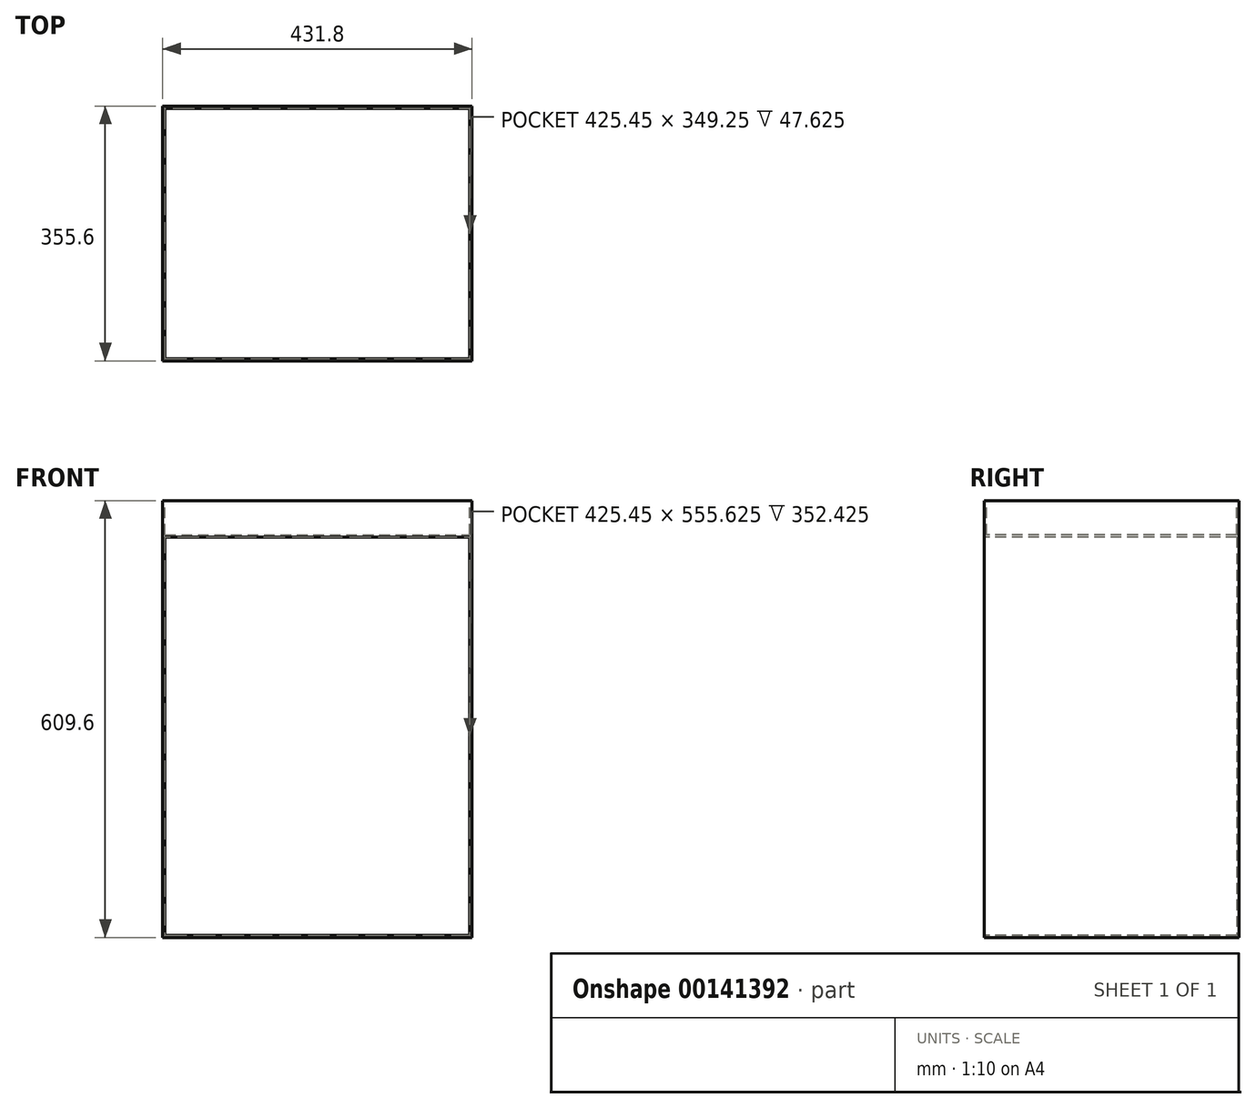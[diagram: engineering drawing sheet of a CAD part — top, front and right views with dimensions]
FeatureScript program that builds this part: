
annotation { "Feature Type Name" : "Feature", "Feature Type Description" : "" }
export const myFeature = defineFeature(function(context is Context, id is Id, definition is map)
    precondition{}
    {
        {
            var Q0;
            Q0=qCreatedBy(makeId("Front.planeOp"),FACE);
            var sketch = newSketch(context, id + "F0", { "sketchPlane" : qUnion([Q0])});
            skLineSegment(sketch, "E0.bottom", {"start": v(-215.9, 304.8) * mm, "end": v(215.9, 304.8) * mm});
            skLineSegment(sketch, "E0.top", {"start": v(-215.9, -304.8) * mm, "end": v(215.9, -304.8) * mm});
            skLineSegment(sketch, "E0.left", {"start": v(-215.9, 304.8) * mm, "end": v(-215.9, -304.8) * mm});
            skLineSegment(sketch, "E0.right", {"start": v(215.9, 304.8) * mm, "end": v(215.9, -304.8) * mm});
            skPoint(sketch, "E0.middle", {"position": v(0, 0) * mm});
            skSolve(sketch);
        }
        {
            var Q0;
            Q0=qSketchRegion(id+"F0",true);
            extrude(context, id + "F1", {"entities" : qUnion([Q0]), "depth" : 355.6 * mm});
        }
        {
            var Q0;
            Q0=makeQuery(id+"F1.opExtrude","CAP_FACE",FACE,{"disambiguationData":[OSD([sQuery(id+"F0.wireOp",EDGE,"E0.bottom"),sQuery(id+"F0.wireOp",EDGE,"E0.top"),sQuery(id+"F0.wireOp",EDGE,"E0.left"),sQuery(id+"F0.wireOp",EDGE,"E0.right")])],"isStart":false});
            var sketch = newSketch(context, id + "F2", { "sketchPlane" : qUnion([Q0])});
            skLineSegment(sketch, "E1.bottom", {"start": v(-212.73, 254) * mm, "end": v(212.72, 254) * mm});
            skLineSegment(sketch, "E1.top", {"start": v(-212.72, -301.62) * mm, "end": v(212.72, -301.62) * mm});
            skLineSegment(sketch, "E1.left", {"start": v(-212.72, 254) * mm, "end": v(-212.73, -301.62) * mm});
            skLineSegment(sketch, "E1.right", {"start": v(212.72, 254) * mm, "end": v(212.73, -301.62) * mm});
            skSolve(sketch);
        }
        {
            var Q0;
            Q0=qSketchRegion(id+"F2",true);
            extrude(context, id + "F3", {"entities" : qUnion([Q0]), "operationType" : NewBodyOperationType.REMOVE, "oppositeDirection" : true, "depth" : 352.42 * mm});
        }
        {
            var Q0;
            Q0=makeQuery(id+"F1.opExtrude","SWEPT_FACE",FACE,{"disambiguationData":[OSD([sQuery(id+"F0.wireOp",EDGE,"E0.bottom")])]});
            var sketch = newSketch(context, id + "F4", { "sketchPlane" : qUnion([Q0])});
            skLineSegment(sketch, "E2.bottom", {"start": v(-212.72, -3.18) * mm, "end": v(212.73, -3.17) * mm});
            skLineSegment(sketch, "E2.top", {"start": v(-212.72, -352.43) * mm, "end": v(212.73, -352.43) * mm});
            skLineSegment(sketch, "E2.left", {"start": v(-212.72, -3.18) * mm, "end": v(-212.72, -352.43) * mm});
            skLineSegment(sketch, "E2.right", {"start": v(212.73, -3.17) * mm, "end": v(212.73, -352.43) * mm});
            skSolve(sketch);
        }
        {
            var Q0;
            Q0=qSketchRegion(id+"F4",true);
            extrude(context, id + "F5", {"entities" : qUnion([Q0]), "operationType" : NewBodyOperationType.REMOVE, "oppositeDirection" : true, "depth" : 47.62 * mm});
        }
    });
